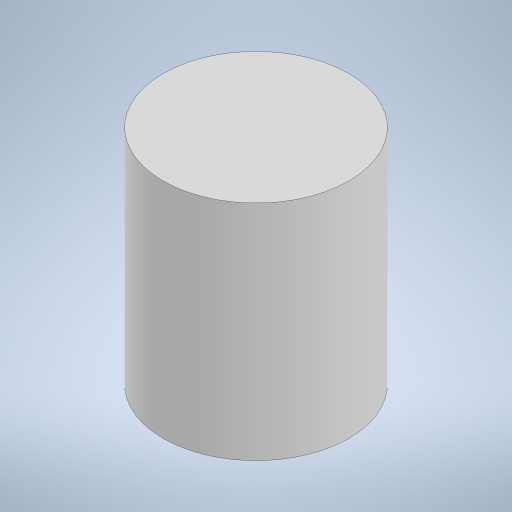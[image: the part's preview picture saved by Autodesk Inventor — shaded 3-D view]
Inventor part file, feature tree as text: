
AUTODESK INVENTOR PART (.ipt)
format: ipt  version: 2023 (Build 270158000, 158)  size: 187,392 bytes
history: native  units: mm
features: extrude x1, sketch x1
ambient origin geometry x8: Origin, YZ Plane, XZ Plane, XY Plane, X Axis, Y Axis, Z Axis, Center Point
bodies: Solid1 (feature_tree)
feature tree (2):
  extrude  "Extrusion1"  Depth=6.0mm TaperAngle=0.0deg
  sketch  "Sketch1"  dims[d0=5.0mm d1=6.0mm d2=0.0mm]
